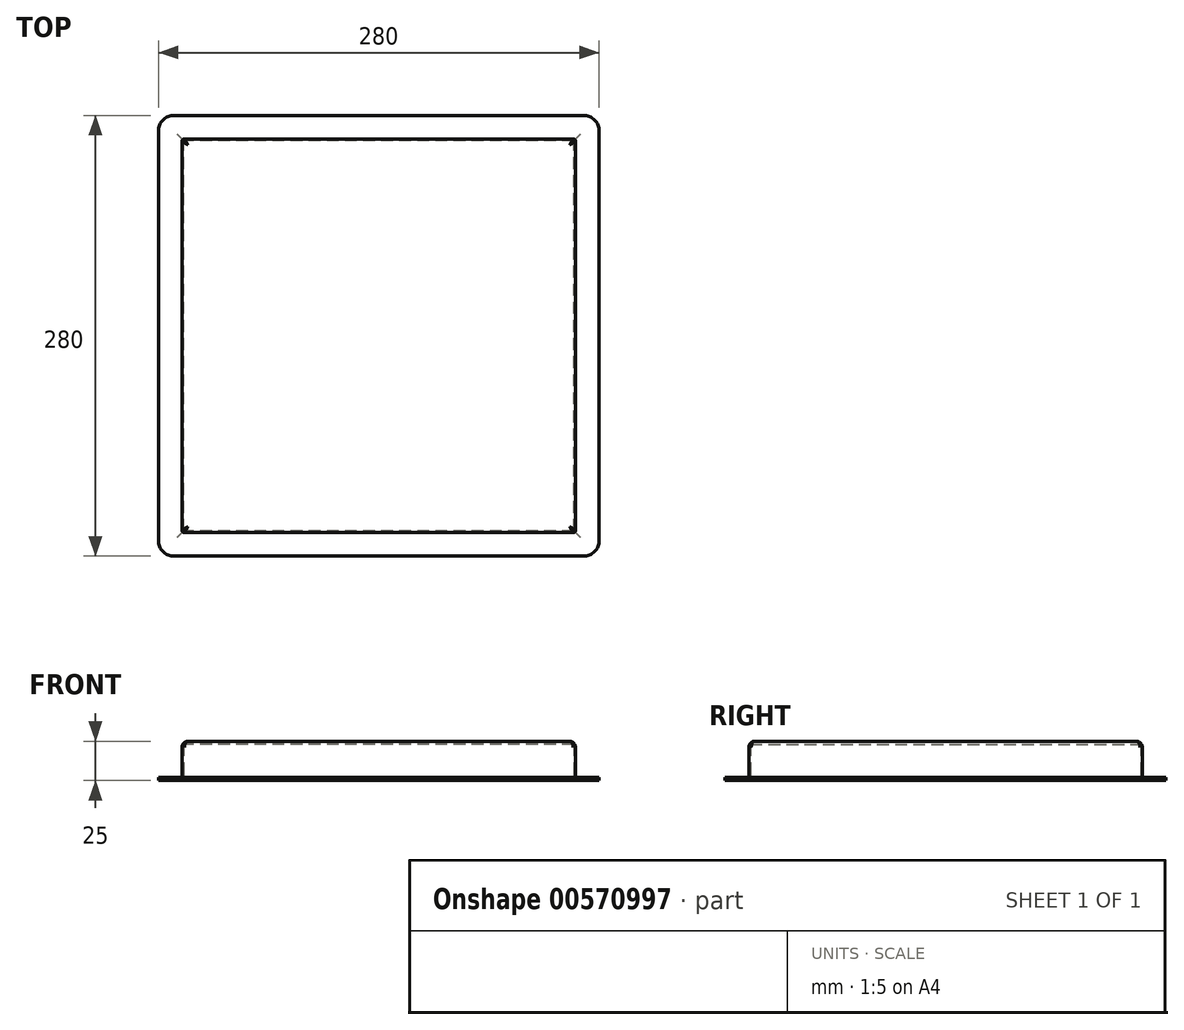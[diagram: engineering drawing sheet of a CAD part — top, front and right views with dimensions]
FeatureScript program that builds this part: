
annotation { "Feature Type Name" : "Feature", "Feature Type Description" : "" }
export const myFeature = defineFeature(function(context is Context, id is Id, definition is map)
    precondition{}
    {
        {
            var Q0;
            Q0=qCreatedBy(makeId("Top.planeOp"),FACE);
            var sketch = newSketch(context, id + "F0", { "sketchPlane" : qUnion([Q0])});
            skLineSegment(sketch, "E0.bottom", {"start": v(125, -125) * mm, "end": v(-125, -125) * mm});
            skLineSegment(sketch, "E0.top", {"start": v(125, 125) * mm, "end": v(-125, 125) * mm});
            skLineSegment(sketch, "E0.left", {"start": v(125, -125) * mm, "end": v(125, 125) * mm});
            skLineSegment(sketch, "E0.right", {"start": v(-125, -125) * mm, "end": v(-125, 125) * mm});
            skPoint(sketch, "E0.middle", {"position": v(0, 0) * mm});
            skLineSegment(sketch, "E1.bottom", {"start": v(124, -124) * mm, "end": v(-124, -124) * mm});
            skLineSegment(sketch, "E1.top", {"start": v(124, 124) * mm, "end": v(-124, 124) * mm});
            skLineSegment(sketch, "E1.left", {"start": v(124, -124) * mm, "end": v(124, 124) * mm});
            skLineSegment(sketch, "E1.right", {"start": v(-124, -124) * mm, "end": v(-124, 124) * mm});
            skLineSegment(sketch, "E2.bottom", {"start": v(130, -140) * mm, "end": v(-130, -140) * mm});
            skLineSegment(sketch, "E2.top", {"start": v(130, 140) * mm, "end": v(-130, 140) * mm});
            skLineSegment(sketch, "E2.left", {"start": v(140, -130) * mm, "end": v(140, 130) * mm});
            skLineSegment(sketch, "E2.right", {"start": v(-140, -130) * mm, "end": v(-140, 130) * mm});
            skPoint(sketch, "E3.visualSharp", {"position": v(-140, 140) * mm});
            skArc(sketch, "E3.filletArc", {"start": v(-130, 140) * mm, "mid": v(-137.07, 137.07) * mm, "end": v(-140, 130) * mm});
            skPoint(sketch, "E4.visualSharp", {"position": v(-140, -140) * mm});
            skArc(sketch, "E4.filletArc", {"start": v(-140, -130) * mm, "mid": v(-137.07, -137.07) * mm, "end": v(-130, -140) * mm});
            skPoint(sketch, "E5.visualSharp", {"position": v(140, -140) * mm});
            skArc(sketch, "E5.filletArc", {"start": v(130, -140) * mm, "mid": v(137.07, -137.07) * mm, "end": v(140, -130) * mm});
            skPoint(sketch, "E6.visualSharp", {"position": v(140, 140) * mm});
            skArc(sketch, "E6.filletArc", {"start": v(140, 130) * mm, "mid": v(137.07, 137.07) * mm, "end": v(130, 140) * mm});
            skSolve(sketch);
        }
        {
            var Q0;
            Q0=makeQuery(id+"F0.imprint","IMPRINT",FACE,{"disambiguationData":[TD([[makeQuery(id+"F0.imprint","IMPRINT",EDGE,{"derivedFrom":sQuery(id+"F0.wireOp",EDGE,"E0.bottom")}),1.0]])]});
            extrude(context, id + "F1", {"entities" : qUnion([Q0]), "depth" : 2 * mm, "offsetDistance" : 25 * mm});
        }
        {
            var Q0;
            Q0=makeQuery(id+"F0.imprint","IMPRINT",FACE,{"disambiguationData":[TD([[makeQuery(id+"F0.imprint","IMPRINT",EDGE,{"derivedFrom":sQuery(id+"F0.wireOp",EDGE,"E0.bottom")}),-1.0]])]});
            extrude(context, id + "F2", {"entities" : qUnion([Q0]), "operationType" : NewBodyOperationType.ADD, "depth" : 25 * mm, "offsetDistance" : 25 * mm});
        }
        {
            var Q0;
            Q0=makeQuery(id+"F2.opExtrude","CAP_FACE",FACE,{"disambiguationData":[OSD([sQuery(id+"F0.wireOp",EDGE,"E0.bottom"),sQuery(id+"F0.wireOp",EDGE,"E0.top"),sQuery(id+"F0.wireOp",EDGE,"E0.left"),sQuery(id+"F0.wireOp",EDGE,"E0.right"),sQuery(id+"F0.wireOp",EDGE,"E1.bottom"),sQuery(id+"F0.wireOp",EDGE,"E1.top"),sQuery(id+"F0.wireOp",EDGE,"E1.left"),sQuery(id+"F0.wireOp",EDGE,"E1.right")])],"isStart":false});
            var sketch = newSketch(context, id + "F3", { "sketchPlane" : qUnion([Q0])});
            skLineSegment(sketch, "E7.bottom", {"start": v(125, -125) * mm, "end": v(-125, -125) * mm});
            skLineSegment(sketch, "E7.top", {"start": v(125, 125) * mm, "end": v(-125, 125) * mm});
            skLineSegment(sketch, "E7.left", {"start": v(125, -125) * mm, "end": v(125, 125) * mm});
            skLineSegment(sketch, "E7.right", {"start": v(-125, -125) * mm, "end": v(-125, 125) * mm});
            skPoint(sketch, "E7.middle", {"position": v(0, 0) * mm});
            skSolve(sketch);
        }
        {
            var Q0;
            Q0=makeQuery(id+"F3.imprint","IMPRINT",FACE,{"disambiguationData":[TD([[makeQuery(id+"F3.imprint","IMPRINT",EDGE,{"derivedFrom":makeQuery(id+"F2.opExtrude","CAP_EDGE",EDGE,{"disambiguationData":[OSD([sQuery(id+"F0.wireOp",EDGE,"E1.bottom")])],"isStart":false})}),-1.0]])]});
            extrude(context, id + "F4", {"entities" : qUnion([Q0]), "operationType" : NewBodyOperationType.ADD, "oppositeDirection" : true, "depth" : 2 * mm, "offsetDistance" : 25 * mm});
        }
        {
            var Q0;
            Q0=makeQuery(id+"F2.opExtrude","CAP_EDGE",EDGE,{"disambiguationData":[OSD([sQuery(id+"F0.wireOp",EDGE,"E1.bottom")])],"isStart":true});
            var Q1;
            Q1=makeQuery(id+"F2.opExtrude","CAP_EDGE",EDGE,{"disambiguationData":[OSD([sQuery(id+"F0.wireOp",EDGE,"E1.right")])],"isStart":true});
            var Q2;
            Q2=makeQuery(id+"F2.opExtrude","CAP_EDGE",EDGE,{"disambiguationData":[OSD([sQuery(id+"F0.wireOp",EDGE,"E1.top")])],"isStart":true});
            var Q3;
            Q3=makeQuery(id+"F2.opExtrude","CAP_EDGE",EDGE,{"disambiguationData":[OSD([sQuery(id+"F0.wireOp",EDGE,"E1.left")])],"isStart":true});
            var Q4;
            Q4=makeQuery(id+"F4.opExtrude","CAP_EDGE",EDGE,{"disambiguationData":[OSD([sQuery(id+"F0.wireOp",EDGE,"E1.bottom")])],"isStart":false});
            var Q5;
            Q5=makeQuery(id+"F4.opExtrude","CAP_EDGE",EDGE,{"disambiguationData":[OSD([sQuery(id+"F0.wireOp",EDGE,"E1.right")])],"isStart":false});
            var Q6;
            Q6=makeQuery(id+"F4.opExtrude","CAP_EDGE",EDGE,{"disambiguationData":[OSD([sQuery(id+"F0.wireOp",EDGE,"E1.left")])],"isStart":false});
            var Q7;
            Q7=makeQuery(id+"F4.opExtrude","CAP_EDGE",EDGE,{"disambiguationData":[OSD([sQuery(id+"F0.wireOp",EDGE,"E1.top")])],"isStart":false});
            var Q8;
            Q8=makeQuery(id+"F2.opExtrude","CAP_EDGE",EDGE,{"disambiguationData":[OSD([sQuery(id+"F0.wireOp",EDGE,"E0.left")])],"isStart":false});
            var Q9;
            Q9=makeQuery(id+"F2.opExtrude","CAP_EDGE",EDGE,{"disambiguationData":[OSD([sQuery(id+"F0.wireOp",EDGE,"E0.top")])],"isStart":false});
            var Q10;
            Q10=makeQuery(id+"F2.opExtrude","CAP_EDGE",EDGE,{"disambiguationData":[OSD([sQuery(id+"F0.wireOp",EDGE,"E0.right")])],"isStart":false});
            var Q11;
            Q11=makeQuery(id+"F2.opExtrude","CAP_EDGE",EDGE,{"disambiguationData":[OSD([sQuery(id+"F0.wireOp",EDGE,"E0.bottom")])],"isStart":false});
            var Q12;
            Q12=makeQuery(id+"F1.opExtrude","CAP_EDGE",EDGE,{"disambiguationData":[OSD([sQuery(id+"F0.wireOp",EDGE,"E0.bottom")])],"isStart":false});
            var Q13;
            Q13=makeQuery(id+"F1.opExtrude","CAP_EDGE",EDGE,{"disambiguationData":[OSD([sQuery(id+"F0.wireOp",EDGE,"E0.left")])],"isStart":false});
            var Q14;
            Q14=makeQuery(id+"F1.opExtrude","CAP_EDGE",EDGE,{"disambiguationData":[OSD([sQuery(id+"F0.wireOp",EDGE,"E0.top")])],"isStart":false});
            var Q15;
            Q15=makeQuery(id+"F1.opExtrude","CAP_EDGE",EDGE,{"disambiguationData":[OSD([sQuery(id+"F0.wireOp",EDGE,"E0.right")])],"isStart":false});
            fillet(context, id + "F5", {"entities" : qUnion([Q0, Q1, Q2, Q3, Q4, Q5, Q6, Q7, Q8, Q9, Q10, Q11, Q12, Q13, Q14, Q15]), "radius" : 4 * mm, "tangentPropagation" : true, "allowEdgeOverflow" : false});
        }
        {
            var Q0;
            Q0=makeQuery(id+"F2.opExtrude","SWEPT_EDGE",EDGE,{"disambiguationData":[OSD([sQuery(id+"F0.wireOp",EDGE,"E0.top"),sQuery(id+"F0.wireOp",EDGE,"E0.right")])]});
            var Q1;
            Q1=makeQuery(id+"F2.opExtrude","SWEPT_EDGE",EDGE,{"disambiguationData":[OSD([sQuery(id+"F0.wireOp",EDGE,"E0.bottom"),sQuery(id+"F0.wireOp",EDGE,"E0.right")])]});
            var Q2;
            Q2=makeQuery(id+"F2.opExtrude","SWEPT_EDGE",EDGE,{"disambiguationData":[OSD([sQuery(id+"F0.wireOp",EDGE,"E0.bottom"),sQuery(id+"F0.wireOp",EDGE,"E0.left")])]});
            var Q3;
            Q3=makeQuery(id+"F2.opExtrude","SWEPT_EDGE",EDGE,{"disambiguationData":[OSD([sQuery(id+"F0.wireOp",EDGE,"E0.top"),sQuery(id+"F0.wireOp",EDGE,"E0.left")])]});
            fillet(context, id + "F6", {"entities" : qUnion([Q0, Q1, Q2, Q3]), "radius" : 1.5 * mm, "tangentPropagation" : true, "allowEdgeOverflow" : false});
        }
    });
